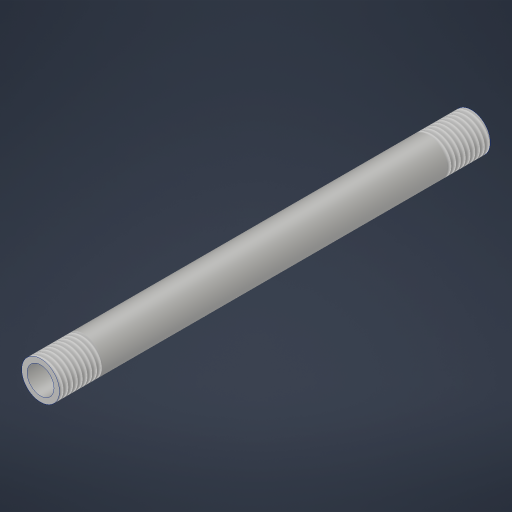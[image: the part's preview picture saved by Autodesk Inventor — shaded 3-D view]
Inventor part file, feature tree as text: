
AUTODESK INVENTOR PART (.ipt)
format: ipt  version: 2023.4 (Build 274418000, 418)  size: 195,584 bytes
history: native  units: in
note: dims shown in document units (in); Inventor stores cm internally (conversion verified against a paired STEP export)
features: thread x2, extrude x1, sketch x1
ambient origin geometry x8: Origin, YZ Plane, XZ Plane, XY Plane, X Axis, Y Axis, Z Axis, Center Point
bodies: Solid1 (feature_tree)
feature tree (4):
  extrude  "Extrusion1"  Depth=10.0in
  thread  "Thread1"  [1 undecoded]
  thread  "Thread2"  [1 undecoded]
  sketch  "Sketch1"  dims[d0=0.875in d1=0.125in d2=10.0in d3=0.0in d4=1.0in d5=0.0in d6=1.0in d7=0.0in]
note: 2 required parameter values undecoded (feature->parameter linkage not recoverable at this tier; creation-order binding heuristic only, values carry confidence <= 0.55)
